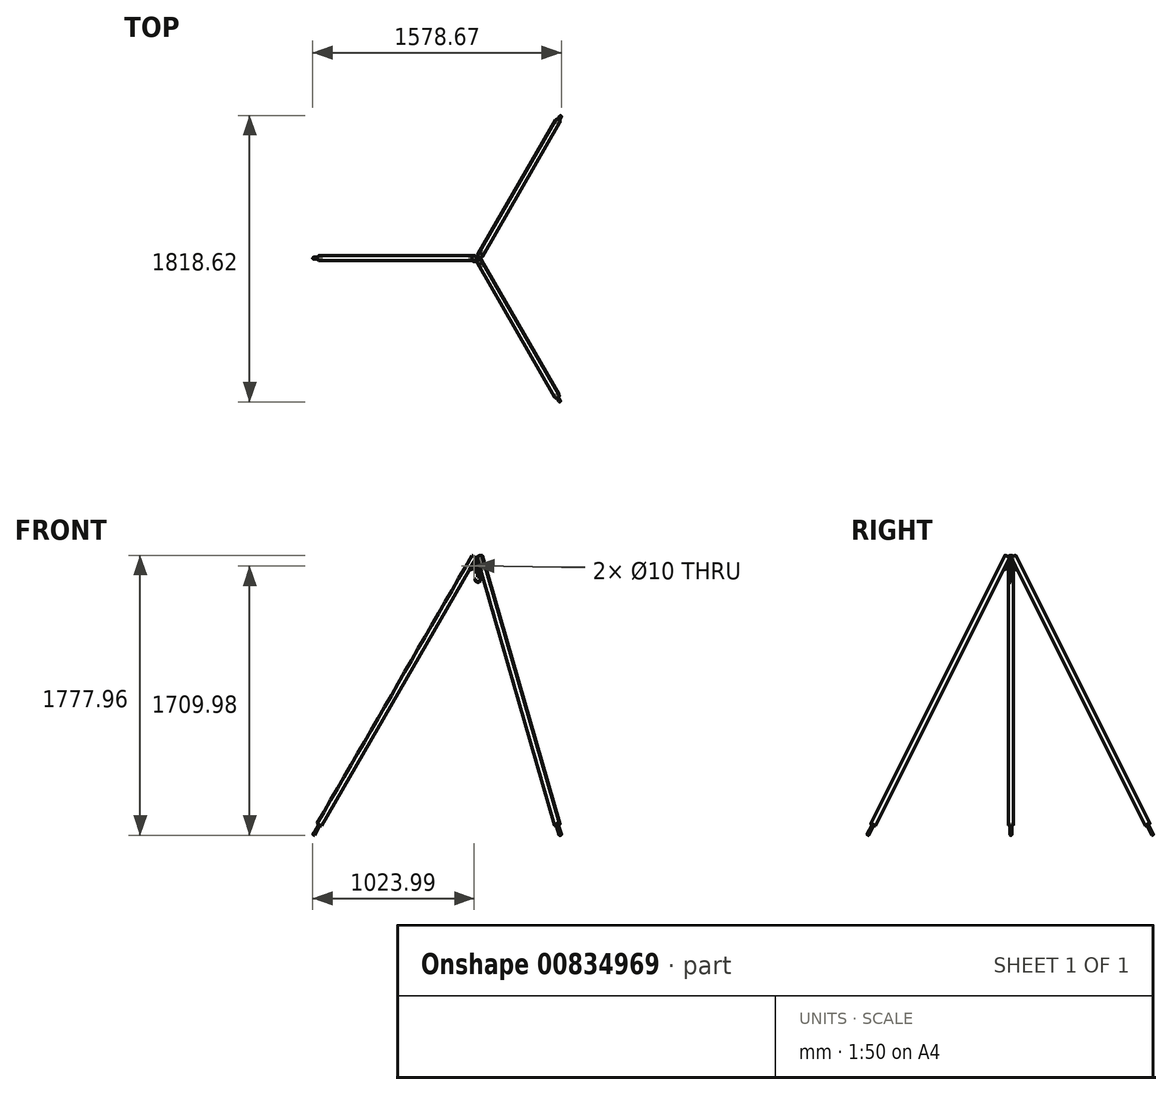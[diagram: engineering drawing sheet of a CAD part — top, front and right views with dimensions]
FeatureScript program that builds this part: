
annotation { "Feature Type Name" : "Feature", "Feature Type Description" : "" }
export const myFeature = defineFeature(function(context is Context, id is Id, definition is map)
    precondition{}
    {
        {
            var Q0;
            Q0=qCreatedBy(makeId("Top.planeOp"),FACE);
            var sketch = newSketch(context, id + "F0", { "sketchPlane" : qUnion([Q0])});
            skCircle(sketch, "E0", {"center": v(0, 0) * mm, "radius": 10 * mm});
            skSolve(sketch);
        }
        {
            var Q0;
            Q0 = qSketchRegion(id + "F0", true);
            extrude(context, id + "F1", {"entities" : qUnion([Q0]), "oppositeDirection" : true, "depth" : 100 * mm, "offsetDistance" : 25 * mm});
        }
        {
            var Q0;
            Q0=qCreatedBy(makeId("Front.planeOp"),FACE);
            var sketch = newSketch(context, id + "F2", { "sketchPlane" : qUnion([Q0])});
            skCircle(sketch, "E1", {"center": v(-25, -51.98) * mm, "radius": 5 * mm});
            skLineSegment(sketch, "E2", {"start": v(-10, 0) * mm, "end": v(-36.26, -45.48) * mm});
            skLineSegment(sketch, "E3", {"start": v(-31.5, -63.24) * mm, "end": v(-10, -75.65) * mm});
            skLineSegment(sketch, "E4", {"start": v(-10, -75.65) * mm, "end": v(-10, 0) * mm});
            skLineSegment(sketch, "E5", {"start": v(-10, -100) * mm, "end": v(-10, 0) * mm, "construction": true});
            skArc(sketch, "E6", {"start": v(-36.26, -45.48) * mm, "mid": v(-37.56, -55.35) * mm, "end": v(-31.5, -63.24) * mm});
            skSolve(sketch);
        }
        {
            var Q0;
            Q0 = qSketchRegion(id + "F2", true);
            extrude(context, id + "F3", {"entities" : qUnion([Q0]), "depth" : 5 * mm, "offsetDistance" : 25 * mm});
        }
        {
            var Q0;
            Q0=makeQuery(id+"F3.opExtrude","SWEPT_BODY",BODY,{"disambiguationData":[OSD([sQuery(id+"F2.wireOp",EDGE,"E1"),sQuery(id+"F2.wireOp",EDGE,"E2"),sQuery(id+"F2.wireOp",EDGE,"E3"),sQuery(id+"F2.wireOp",EDGE,"E4"),sQuery(id+"F2.wireOp",EDGE,"E6")])]});
            var Q1;
            Q1=makeQuery(id+"F1.opExtrude","CAP_EDGE",EDGE,{"disambiguationData":[OSD([sQuery(id+"F0.wireOp",EDGE,"E0")])],"isStart":true});
            circularPattern(context, id + "F4", {"entities" : qUnion([Q0]), "axis" : qUnion([Q1]), "angle" : 360 * degree, "instanceCount" : 3, "equalSpace" : true});
        }
        {
            var Q0;
            Q0=makeQuery(id+"F3.opExtrude","CAP_FACE",FACE,{"disambiguationData":[OSD([sQuery(id+"F2.wireOp",EDGE,"E1"),sQuery(id+"F2.wireOp",EDGE,"E2"),sQuery(id+"F2.wireOp",EDGE,"E3"),sQuery(id+"F2.wireOp",EDGE,"E4"),sQuery(id+"F2.wireOp",EDGE,"E6")])],"isStart":true});
            var sketch = newSketch(context, id + "F5", { "sketchPlane" : qUnion([Q0])});
            skCircle(sketch, "E7.0", {"center": v(25, -51.98) * mm, "radius": 5 * mm});
            skLineSegment(sketch, "E8", {"start": v(12.16, -3.74) * mm, "end": v(56.42, -80.4) * mm});
            skArc(sketch, "E9", {"start": v(12.16, -51.98) * mm, "mid": v(14.2, -58.93) * mm, "end": v(19.68, -63.67) * mm});
            skLineSegment(sketch, "E10", {"start": v(12.16, -51.98) * mm, "end": v(12.16, -3.74) * mm});
            skLineSegment(sketch, "E11", {"start": v(19.68, -63.67) * mm, "end": v(56.42, -80.4) * mm});
            skSolve(sketch);
        }
        {
            var Q0;
            Q0 = qSketchRegion(id + "F5", true);
            extrude(context, id + "F6", {"entities" : qUnion([Q0]), "depth" : 5 * mm, "offsetDistance" : 25 * mm});
        }
        {
            var Q0;
            Q0=makeQuery(id+"F3.opExtrude","SWEPT_FACE",FACE,{"disambiguationData":[OSD([sQuery(id+"F2.wireOp",EDGE,"E3")])]});
            var sketch = newSketch(context, id + "F7", { "sketchPlane" : qUnion([Q0])});
            skCircle(sketch, "E12", {"center": v(-24.66, -2.5) * mm, "radius": 16 * mm});
            skLineSegment(sketch, "E13", {"start": v(13.3, -5) * mm, "end": v(-29.67, -5) * mm, "construction": true});
            skLineSegment(sketch, "E14", {"start": v(12.97, 0) * mm, "end": v(-28.4, 0) * mm, "construction": true});
            skLineSegment(sketch, "E15", {"start": v(-24.66, -2.5) * mm, "end": v(-30.84, -2.5) * mm, "construction": true});
            skSolve(sketch);
        }
        {
            var Q0;
            Q0 = qSketchRegion(id + "F7", true);
            var Q1;
            Q1=makeQuery(id+"F3.opExtrude","CAP_VERTEX",VERTEX,{"disambiguationData":[OSD([sQuery(id+"F2.wireOp",EDGE,"E2"),sQuery(id+"F2.wireOp",EDGE,"E4")])],"isStart":true});
            extrude(context, id + "F8", {"entities" : qUnion([Q0]), "endBound" : BoundingType.UP_TO_VERTEX, "oppositeDirection" : true, "depth" : 25 * mm, "endBoundEntityVertex" : qUnion([Q1]), "offsetDistance" : 25 * mm, "hasSecondDirection" : true, "secondDirectionOppositeDirection" : false, "secondDirectionDepth" : 1900 * mm});
        }
        {
            var Q0;
            Q0=makeQuery(id+"F8.opExtrude","CAP_FACE",FACE,{"disambiguationData":[OSD([sQuery(id+"F7.wireOp",EDGE,"E12")])],"isStart":true});
            var sketch = newSketch(context, id + "F9", { "sketchPlane" : qUnion([Q0])});
            skCircle(sketch, "E16", {"center": v(-24.66, -2.5) * mm, "radius": 5.63 * mm});
            skSolve(sketch);
        }
        {
            var Q0;
            Q0 = qSketchRegion(id + "F9", true);
            extrude(context, id + "F10", {"entities" : qUnion([Q0]), "operationType" : NewBodyOperationType.ADD, "depth" : 75 * mm, "offsetDistance" : 25 * mm});
        }
        {
            var Q0;
            Q0=makeQuery(id+"F6.opExtrude","SWEPT_BODY",BODY,{"disambiguationData":[OSD([sQuery(id+"F5.wireOp",EDGE,"E7.0"),sQuery(id+"F5.wireOp",EDGE,"E8"),sQuery(id+"F5.wireOp",EDGE,"E9"),sQuery(id+"F5.wireOp",EDGE,"E10"),sQuery(id+"F5.wireOp",EDGE,"E11")])]});
            var Q1;
            Q1=makeQuery(id+"F1.opExtrude","CAP_EDGE",EDGE,{"disambiguationData":[OSD([sQuery(id+"F0.wireOp",EDGE,"E0")])],"isStart":true});
            circularPattern(context, id + "F11", {"entities" : qUnion([Q0]), "axis" : qUnion([Q1]), "angle" : 360 * degree, "instanceCount" : 3, "equalSpace" : true});
        }
        {
            var Q0;
            Q0=makeQuery(id+"F8.opExtrude","SWEPT_BODY",BODY,{"disambiguationData":[OSD([sQuery(id+"F7.wireOp",EDGE,"E12")])]});
            var Q1;
            Q1=makeQuery(id+"F1.opExtrude","CAP_EDGE",EDGE,{"disambiguationData":[OSD([sQuery(id+"F0.wireOp",EDGE,"E0")])],"isStart":true});
            circularPattern(context, id + "F12", {"entities" : qUnion([Q0]), "axis" : qUnion([Q1]), "angle" : 360 * degree, "instanceCount" : 3, "equalSpace" : true});
        }
        {
            var Q0;
            Q0=qCreatedBy(makeId("Front.planeOp"),FACE);
            var sketch = newSketch(context, id + "F13", { "sketchPlane" : qUnion([Q0])});
            skLineSegment(sketch, "E17.0", {"start": v(-10, -100) * mm, "end": v(10, -100) * mm, "construction": true});
            skLineSegment(sketch, "E18", {"start": v(0, -100) * mm, "end": v(0, -169.58) * mm, "construction": true});
            skArc(sketch, "E19", {"start": v(2.5, -114.95) * mm, "mid": v(13.23, -149.8) * mm, "end": v(-20, -134.8) * mm});
            skArc(sketch, "E20", {"start": v(-2.5, -120) * mm, "mid": v(11.46, -144.47) * mm, "end": v(-15, -134.8) * mm});
            skLineSegment(sketch, "E21", {"start": v(2.5, -114.95) * mm, "end": v(2.5, -100) * mm});
            skLineSegment(sketch, "E22", {"start": v(2.5, -100) * mm, "end": v(-2.5, -100) * mm});
            skLineSegment(sketch, "E23", {"start": v(-2.5, -100) * mm, "end": v(-2.5, -120) * mm});
            skLineSegment(sketch, "E24", {"start": v(-15, -134.8) * mm, "end": v(-20, -134.8) * mm});
            skSolve(sketch);
        }
        {
            var Q0;
            Q0 = qSketchRegion(id + "F13", true);
            extrude(context, id + "F14", {"entities" : qUnion([Q0]), "operationType" : NewBodyOperationType.ADD, "endBound" : BoundingType.SYMMETRIC, "depth" : 5 * mm, "offsetDistance" : 25 * mm});
        }
        {
            var Q0;
            Q0=makeQuery(id+"F6.opExtrude","CAP_FACE",FACE,{"disambiguationData":[OSD([sQuery(id+"F5.wireOp",EDGE,"E7.0"),sQuery(id+"F5.wireOp",EDGE,"E8"),sQuery(id+"F5.wireOp",EDGE,"E9"),sQuery(id+"F5.wireOp",EDGE,"E10"),sQuery(id+"F5.wireOp",EDGE,"E11")])],"isStart":false});
            var sketch = newSketch(context, id + "F15", { "sketchPlane" : qUnion([Q0])});
            skCircle(sketch, "E25.0", {"center": v(25, -51.98) * mm, "radius": 5 * mm});
            skSolve(sketch);
        }
        {
            var Q0;
            Q0 = qSketchRegion(id + "F15", true);
            extrude(context, id + "F16", {"entities" : qUnion([Q0]), "oppositeDirection" : true, "depth" : 25 * mm, "offsetDistance" : 25 * mm});
        }
        {
            var Q0;
            Q0=makeQuery(id+"F3.opExtrude","CAP_FACE",FACE,{"disambiguationData":[OSD([sQuery(id+"F2.wireOp",EDGE,"E1"),sQuery(id+"F2.wireOp",EDGE,"E2"),sQuery(id+"F2.wireOp",EDGE,"E3"),sQuery(id+"F2.wireOp",EDGE,"E4"),sQuery(id+"F2.wireOp",EDGE,"E6")])],"isStart":false});
            var sketch = newSketch(context, id + "F17", { "sketchPlane" : qUnion([Q0])});
            skCircle(sketch, "E26.0", {"center": v(-25, -51.98) * mm, "radius": 5 * mm});
            skCircle(sketch, "E27.cCircle", {"center": v(-25, -51.98) * mm, "radius": 8.5 * mm, "construction": true});
            skLineSegment(sketch, "E27.0", {"start": v(-16.12, -56.15) * mm, "end": v(-24.17, -61.76) * mm});
            skLineSegment(sketch, "E27.1", {"start": v(-24.17, -61.76) * mm, "end": v(-33.05, -57.59) * mm});
            skLineSegment(sketch, "E27.2", {"start": v(-33.05, -57.59) * mm, "end": v(-33.88, -47.8) * mm});
            skLineSegment(sketch, "E27.3", {"start": v(-33.88, -47.8) * mm, "end": v(-25.83, -42.2) * mm});
            skLineSegment(sketch, "E27.4", {"start": v(-25.83, -42.2) * mm, "end": v(-16.95, -46.37) * mm});
            skLineSegment(sketch, "E27.5", {"start": v(-16.95, -46.37) * mm, "end": v(-16.12, -56.15) * mm});
            skPoint(sketch, "E27.0.midPoint", {"position": v(-20.14, -58.96) * mm});
            skSolve(sketch);
        }
        {
            var Q0;
            Q0 = qSketchRegion(id + "F17", true);
            extrude(context, id + "F18", {"entities" : qUnion([Q0]), "depth" : 10 * mm, "offsetDistance" : 25 * mm});
        }
        {
            var Q0;
            Q0=makeQuery(id+"F16.opExtrude","CAP_FACE",FACE,{"disambiguationData":[OSD([sQuery(id+"F15.wireOp",EDGE,"E25.0")])],"isStart":true});
            var sketch = newSketch(context, id + "F19", { "sketchPlane" : qUnion([Q0])});
            skCircle(sketch, "E28.cCircle", {"center": v(25, -51.98) * mm, "radius": 8.5 * mm, "construction": true});
            skLineSegment(sketch, "E28.0", {"start": v(34.78, -52.75) * mm, "end": v(29.22, -60.84) * mm});
            skLineSegment(sketch, "E28.1", {"start": v(29.22, -60.84) * mm, "end": v(19.44, -60.07) * mm});
            skLineSegment(sketch, "E28.2", {"start": v(19.44, -60.07) * mm, "end": v(15.22, -51.2) * mm});
            skLineSegment(sketch, "E28.3", {"start": v(15.22, -51.2) * mm, "end": v(20.78, -43.12) * mm});
            skLineSegment(sketch, "E28.4", {"start": v(20.78, -43.12) * mm, "end": v(30.56, -43.9) * mm});
            skLineSegment(sketch, "E28.5", {"start": v(30.56, -43.9) * mm, "end": v(34.78, -52.75) * mm});
            skPoint(sketch, "E28.0.midPoint", {"position": v(32, -56.8) * mm});
            skSolve(sketch);
        }
        {
            var Q0;
            Q0 = qSketchRegion(id + "F19", true);
            extrude(context, id + "F20", {"entities" : qUnion([Q0]), "operationType" : NewBodyOperationType.ADD, "depth" : 10 * mm, "offsetDistance" : 25 * mm});
        }
        {
            var Q0;
            Q0=makeQuery(id+"F16.opExtrude","SWEPT_BODY",BODY,{"disambiguationData":[OSD([sQuery(id+"F15.wireOp",EDGE,"E25.0")])]});
            var Q1;
            Q1=makeQuery(id+"F18.opExtrude","SWEPT_BODY",BODY,{"disambiguationData":[OSD([sQuery(id+"F17.wireOp",EDGE,"E26.0"),sQuery(id+"F17.wireOp",EDGE,"E27.0"),sQuery(id+"F17.wireOp",EDGE,"E27.1"),sQuery(id+"F17.wireOp",EDGE,"E27.2"),sQuery(id+"F17.wireOp",EDGE,"E27.3"),sQuery(id+"F17.wireOp",EDGE,"E27.4"),sQuery(id+"F17.wireOp",EDGE,"E27.5")])]});
            var Q2;
            Q2=makeQuery(id+"F1.opExtrude","CAP_EDGE",EDGE,{"disambiguationData":[OSD([sQuery(id+"F0.wireOp",EDGE,"E0")])],"isStart":true});
            circularPattern(context, id + "F21", {"entities" : qUnion([Q0, Q1]), "axis" : qUnion([Q2]), "angle" : 360 * degree, "instanceCount" : 3, "equalSpace" : true});
        }
    });
